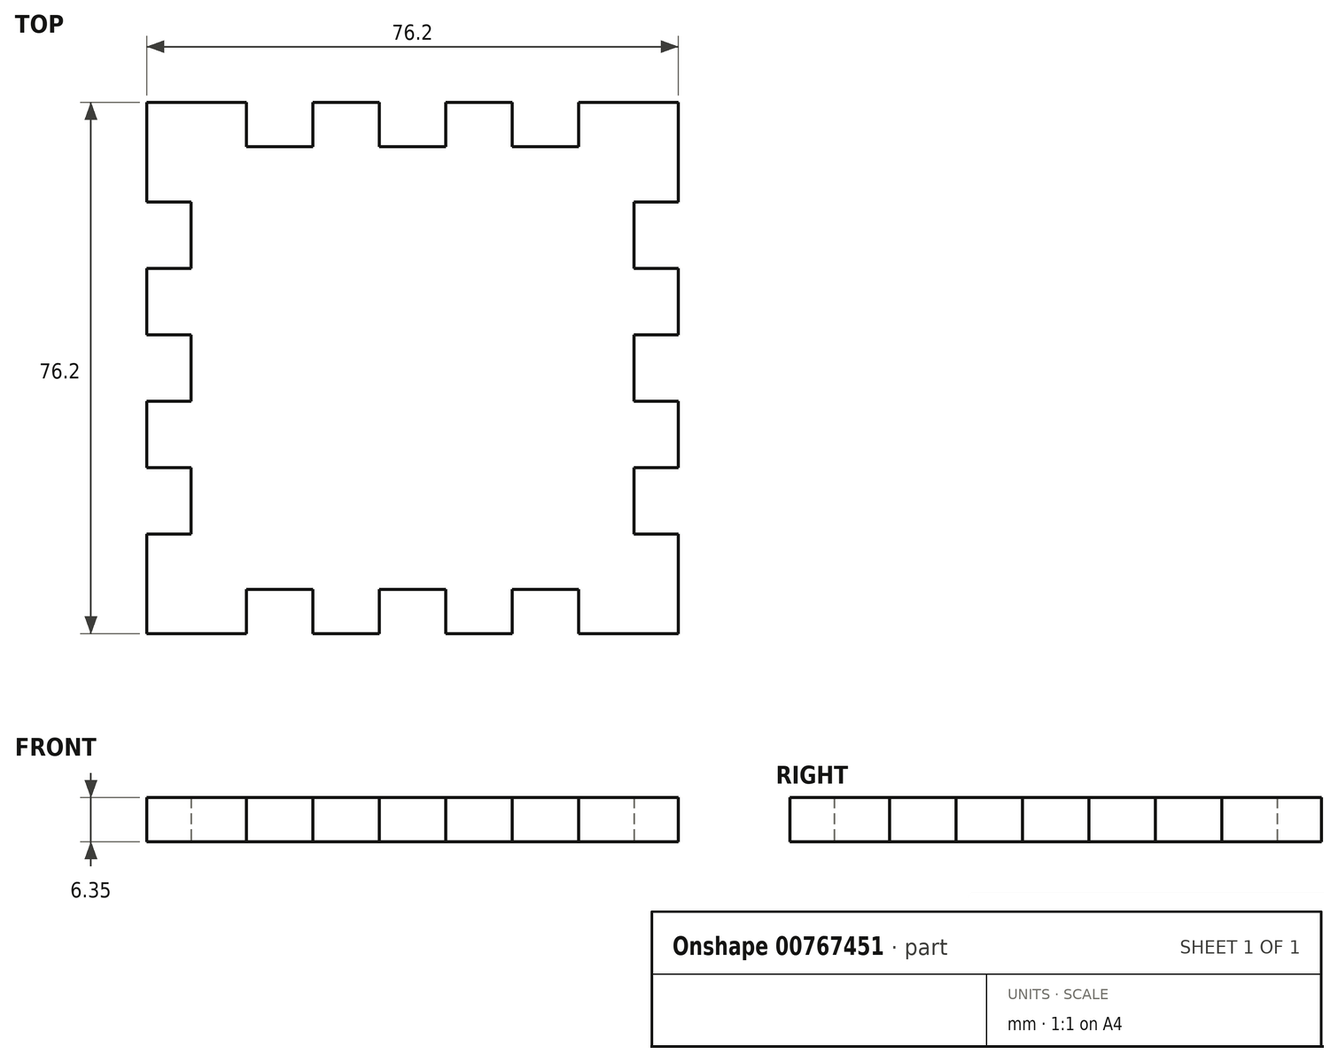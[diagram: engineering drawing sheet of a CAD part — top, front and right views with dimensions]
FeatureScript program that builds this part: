
annotation { "Feature Type Name" : "Feature", "Feature Type Description" : "" }
export const myFeature = defineFeature(function(context is Context, id is Id, definition is map)
    precondition{}
    {
        {
            var Q0;
            Q0=qCreatedBy(makeId("Top.planeOp"),FACE);
            var sketch = newSketch(context, id + "F0", { "sketchPlane" : qUnion([Q0])});
            skLineSegment(sketch, "E0.bottom", {"start": v(0, 0) * mm, "end": v(76.2, 0) * mm});
            skLineSegment(sketch, "E0.top", {"start": v(0, -76.2) * mm, "end": v(76.2, -76.2) * mm});
            skLineSegment(sketch, "E0.left", {"start": v(0, 0) * mm, "end": v(0, -76.2) * mm});
            skLineSegment(sketch, "E0.right", {"start": v(76.2, 0) * mm, "end": v(76.2, -76.2) * mm});
            skLineSegment(sketch, "E1.bottom", {"start": v(14.29, 0) * mm, "end": v(23.81, 0) * mm});
            skLineSegment(sketch, "E1.top", {"start": v(14.29, -6.35) * mm, "end": v(23.81, -6.35) * mm});
            skLineSegment(sketch, "E1.left", {"start": v(14.29, 0) * mm, "end": v(14.29, -6.35) * mm});
            skLineSegment(sketch, "E1.right", {"start": v(23.81, 0) * mm, "end": v(23.81, -6.35) * mm});
            skLineSegment(sketch, "E2.bottom", {"start": v(33.34, 0) * mm, "end": v(42.86, 0) * mm});
            skLineSegment(sketch, "E2.top", {"start": v(33.34, -6.35) * mm, "end": v(42.86, -6.35) * mm});
            skLineSegment(sketch, "E2.left", {"start": v(33.34, 0) * mm, "end": v(33.34, -6.35) * mm});
            skLineSegment(sketch, "E2.right", {"start": v(42.86, 0) * mm, "end": v(42.86, -6.35) * mm});
            skLineSegment(sketch, "E3.bottom", {"start": v(52.39, 0) * mm, "end": v(61.91, 0) * mm});
            skLineSegment(sketch, "E3.top", {"start": v(52.39, -6.35) * mm, "end": v(61.91, -6.35) * mm});
            skLineSegment(sketch, "E3.left", {"start": v(52.39, 0) * mm, "end": v(52.39, -6.35) * mm});
            skLineSegment(sketch, "E3.right", {"start": v(61.91, 0) * mm, "end": v(61.91, -6.35) * mm});
            skLineSegment(sketch, "E4", {"start": v(23.81, -6.35) * mm, "end": v(33.34, -6.35) * mm, "construction": true});
            skLineSegment(sketch, "E5", {"start": v(42.86, -6.35) * mm, "end": v(52.39, -6.35) * mm, "construction": true});
            skLineSegment(sketch, "E6", {"start": v(0, -6.35) * mm, "end": v(14.29, -6.35) * mm, "construction": true});
            skLineSegment(sketch, "E7", {"start": v(61.91, -6.35) * mm, "end": v(76.2, -6.35) * mm, "construction": true});
            skLineSegment(sketch, "E8.bottom", {"start": v(0, -14.29) * mm, "end": v(6.35, -14.29) * mm});
            skLineSegment(sketch, "E8.top", {"start": v(0, -23.81) * mm, "end": v(6.35, -23.81) * mm});
            skLineSegment(sketch, "E8.left", {"start": v(0, -14.29) * mm, "end": v(0, -23.81) * mm});
            skLineSegment(sketch, "E8.right", {"start": v(6.35, -14.29) * mm, "end": v(6.35, -23.81) * mm});
            skLineSegment(sketch, "E9.bottom", {"start": v(0, -33.34) * mm, "end": v(6.35, -33.34) * mm});
            skLineSegment(sketch, "E9.top", {"start": v(0, -42.86) * mm, "end": v(6.35, -42.86) * mm});
            skLineSegment(sketch, "E9.left", {"start": v(0, -33.34) * mm, "end": v(0, -42.86) * mm});
            skLineSegment(sketch, "E9.right", {"start": v(6.35, -33.34) * mm, "end": v(6.35, -42.86) * mm});
            skLineSegment(sketch, "E10.bottom", {"start": v(0, -52.39) * mm, "end": v(6.35, -52.39) * mm});
            skLineSegment(sketch, "E10.top", {"start": v(0, -61.91) * mm, "end": v(6.35, -61.91) * mm});
            skLineSegment(sketch, "E10.left", {"start": v(0, -52.39) * mm, "end": v(0, -61.91) * mm});
            skLineSegment(sketch, "E10.right", {"start": v(6.35, -52.39) * mm, "end": v(6.35, -61.91) * mm});
            skLineSegment(sketch, "E11", {"start": v(6.35, -14.29) * mm, "end": v(6.35, 0) * mm, "construction": true});
            skLineSegment(sketch, "E12", {"start": v(6.35, -23.81) * mm, "end": v(6.35, -33.34) * mm, "construction": true});
            skLineSegment(sketch, "E13", {"start": v(6.35, -42.86) * mm, "end": v(6.35, -52.39) * mm, "construction": true});
            skLineSegment(sketch, "E14", {"start": v(6.35, -61.91) * mm, "end": v(6.35, -76.2) * mm, "construction": true});
            skLineSegment(sketch, "E15", {"start": v(0, -76.2) * mm, "end": v(76.2, 0) * mm, "construction": true});
            skLineSegment(sketch, "E16.MirrorCS", {"start": v(76.2, -61.91) * mm, "end": v(69.85, -61.91) * mm});
            skLineSegment(sketch, "E17.MirrorCS", {"start": v(69.85, -61.91) * mm, "end": v(69.85, -52.39) * mm});
            skLineSegment(sketch, "E18.MirrorCS", {"start": v(76.2, -52.39) * mm, "end": v(69.85, -52.39) * mm});
            skLineSegment(sketch, "E19.MirrorCS", {"start": v(76.2, -42.86) * mm, "end": v(69.85, -42.86) * mm});
            skLineSegment(sketch, "E20.MirrorCS", {"start": v(69.85, -42.86) * mm, "end": v(69.85, -33.34) * mm});
            skLineSegment(sketch, "E21.MirrorCS", {"start": v(76.2, -33.34) * mm, "end": v(69.85, -33.34) * mm});
            skLineSegment(sketch, "E22.MirrorCS", {"start": v(69.85, -23.81) * mm, "end": v(69.85, -14.29) * mm});
            skLineSegment(sketch, "E23.MirrorCS", {"start": v(76.2, -14.29) * mm, "end": v(69.85, -14.29) * mm});
            skLineSegment(sketch, "E24.MirrorCS", {"start": v(76.2, -23.81) * mm, "end": v(69.85, -23.81) * mm});
            skLineSegment(sketch, "E25.MirrorCS", {"start": v(61.91, -76.2) * mm, "end": v(61.91, -69.85) * mm});
            skLineSegment(sketch, "E26.MirrorCS", {"start": v(61.91, -69.85) * mm, "end": v(52.39, -69.85) * mm});
            skLineSegment(sketch, "E27.MirrorCS", {"start": v(52.39, -76.2) * mm, "end": v(52.39, -69.85) * mm});
            skLineSegment(sketch, "E28.MirrorCS", {"start": v(42.86, -76.2) * mm, "end": v(42.86, -69.85) * mm});
            skLineSegment(sketch, "E29.MirrorCS", {"start": v(42.86, -69.85) * mm, "end": v(33.34, -69.85) * mm});
            skLineSegment(sketch, "E30.MirrorCS", {"start": v(33.34, -76.2) * mm, "end": v(33.34, -69.85) * mm});
            skLineSegment(sketch, "E31.MirrorCS", {"start": v(23.81, -76.2) * mm, "end": v(23.81, -69.85) * mm});
            skLineSegment(sketch, "E32.MirrorCS", {"start": v(23.81, -69.85) * mm, "end": v(14.29, -69.85) * mm});
            skLineSegment(sketch, "E33.MirrorCS", {"start": v(14.29, -76.2) * mm, "end": v(14.29, -69.85) * mm});
            skSolve(sketch);
        }
        {
            var Q0;
            Q0=makeQuery(id+"F0.imprint","IMPRINT",FACE,{"disambiguationData":[TD([[makeQuery(id+"F0.imprint","IMPRINT",EDGE,{"derivedFrom":sQuery(id+"F0.wireOp",EDGE,"E1.top")}),-1.0]])]});
            extrude(context, id + "F1", {"entities" : qUnion([Q0]), "depth" : 6.35 * mm, "offsetDistance" : 25.4 * mm});
        }
    });
